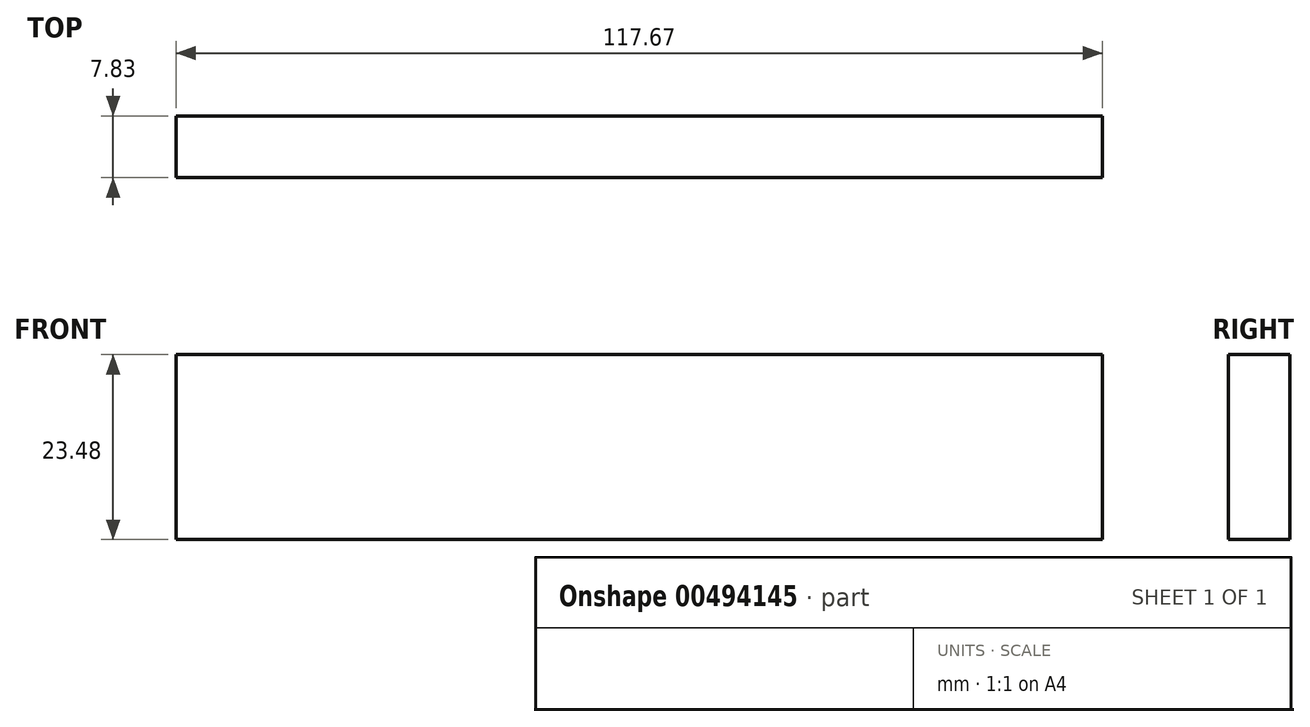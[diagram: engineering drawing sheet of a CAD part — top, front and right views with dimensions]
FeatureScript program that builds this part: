
annotation { "Feature Type Name" : "Feature", "Feature Type Description" : "" }
export const myFeature = defineFeature(function(context is Context, id is Id, definition is map)
    precondition{}
    {
        {
            var Q0;
            Q0=qCreatedBy(makeId("Front.planeOp"),FACE);
            var sketch = newSketch(context, id + "F0", { "sketchPlane" : qUnion([Q0])});
            skLineSegment(sketch, "E0.bottom", {"start": v(-59.1, 23.48) * mm, "end": v(58.56, 23.48) * mm});
            skLineSegment(sketch, "E0.top", {"start": v(-59.1, 0) * mm, "end": v(58.56, 0) * mm});
            skLineSegment(sketch, "E0.left", {"start": v(-59.1, 23.48) * mm, "end": v(-59.1, 0) * mm});
            skLineSegment(sketch, "E0.right", {"start": v(58.56, 23.48) * mm, "end": v(58.56, 0) * mm});
            skSolve(sketch);
        }
        {
            var Q0;
            Q0=makeQuery(id+"F0.imprint","IMPRINT",FACE,{"disambiguationData":[TD([[makeQuery(id+"F0.imprint","IMPRINT",EDGE,{"derivedFrom":sQuery(id+"F0.wireOp",EDGE,"E0.bottom")}),-1.0]])]});
            extrude(context, id + "F1", {"entities" : qUnion([Q0]), "depth" : 7.83 * mm});
        }
    });
